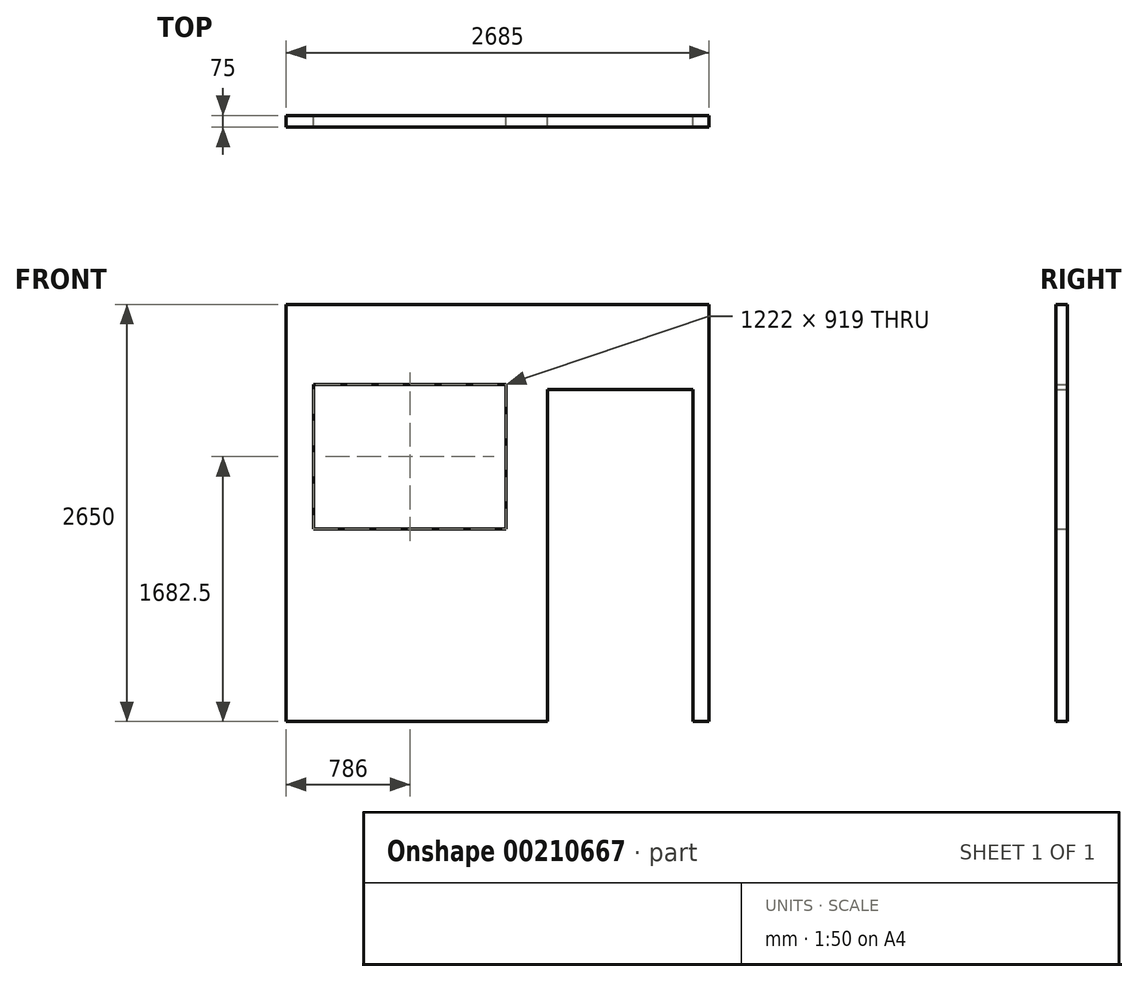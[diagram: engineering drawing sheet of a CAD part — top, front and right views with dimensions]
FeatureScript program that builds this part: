
annotation { "Feature Type Name" : "Feature", "Feature Type Description" : "" }
export const myFeature = defineFeature(function(context is Context, id is Id, definition is map)
    precondition{}
    {
        {
            var Q0;
            Q0=qCreatedBy(makeId("Front.planeOp"),FACE);
            var sketch = newSketch(context, id + "F0", { "sketchPlane" : qUnion([Q0])});
            skLineSegment(sketch, "E0.bottom", {"start": v(0, 0) * mm, "end": v(2685, 0) * mm});
            skLineSegment(sketch, "E0.top", {"start": v(0, 2650) * mm, "end": v(2685, 2650) * mm});
            skLineSegment(sketch, "E0.left", {"start": v(0, 0) * mm, "end": v(0, 2650) * mm});
            skLineSegment(sketch, "E0.right", {"start": v(2685, 0) * mm, "end": v(2685, 2650) * mm});
            skLineSegment(sketch, "E1.bottom", {"start": v(1660, 0) * mm, "end": v(2585, 0) * mm});
            skLineSegment(sketch, "E1.top", {"start": v(1660, 2110) * mm, "end": v(2585, 2110) * mm});
            skLineSegment(sketch, "E1.left", {"start": v(1660, 0) * mm, "end": v(1660, 2110) * mm});
            skLineSegment(sketch, "E1.right", {"start": v(2585, 0) * mm, "end": v(2585, 2110) * mm});
            skLineSegment(sketch, "E2.bottom", {"start": v(175, 2142) * mm, "end": v(1397, 2142) * mm});
            skLineSegment(sketch, "E2.top", {"start": v(175, 1223) * mm, "end": v(1397, 1223) * mm});
            skLineSegment(sketch, "E2.left", {"start": v(175, 2142) * mm, "end": v(175, 1223) * mm});
            skLineSegment(sketch, "E2.right", {"start": v(1397, 2142) * mm, "end": v(1397, 1223) * mm});
            skSolve(sketch);
        }
        {
            var Q0;
            Q0=makeQuery(id+"F0.imprint","IMPRINT",FACE,{"disambiguationData":[TD([[makeQuery(id+"F0.imprint","IMPRINT",EDGE,{"derivedFrom":sQuery(id+"F0.wireOp",EDGE,"E0.bottom")}),1.0]])]});
            extrude(context, id + "F1", {"entities" : qUnion([Q0]), "depth" : 75 * mm});
        }
    });
